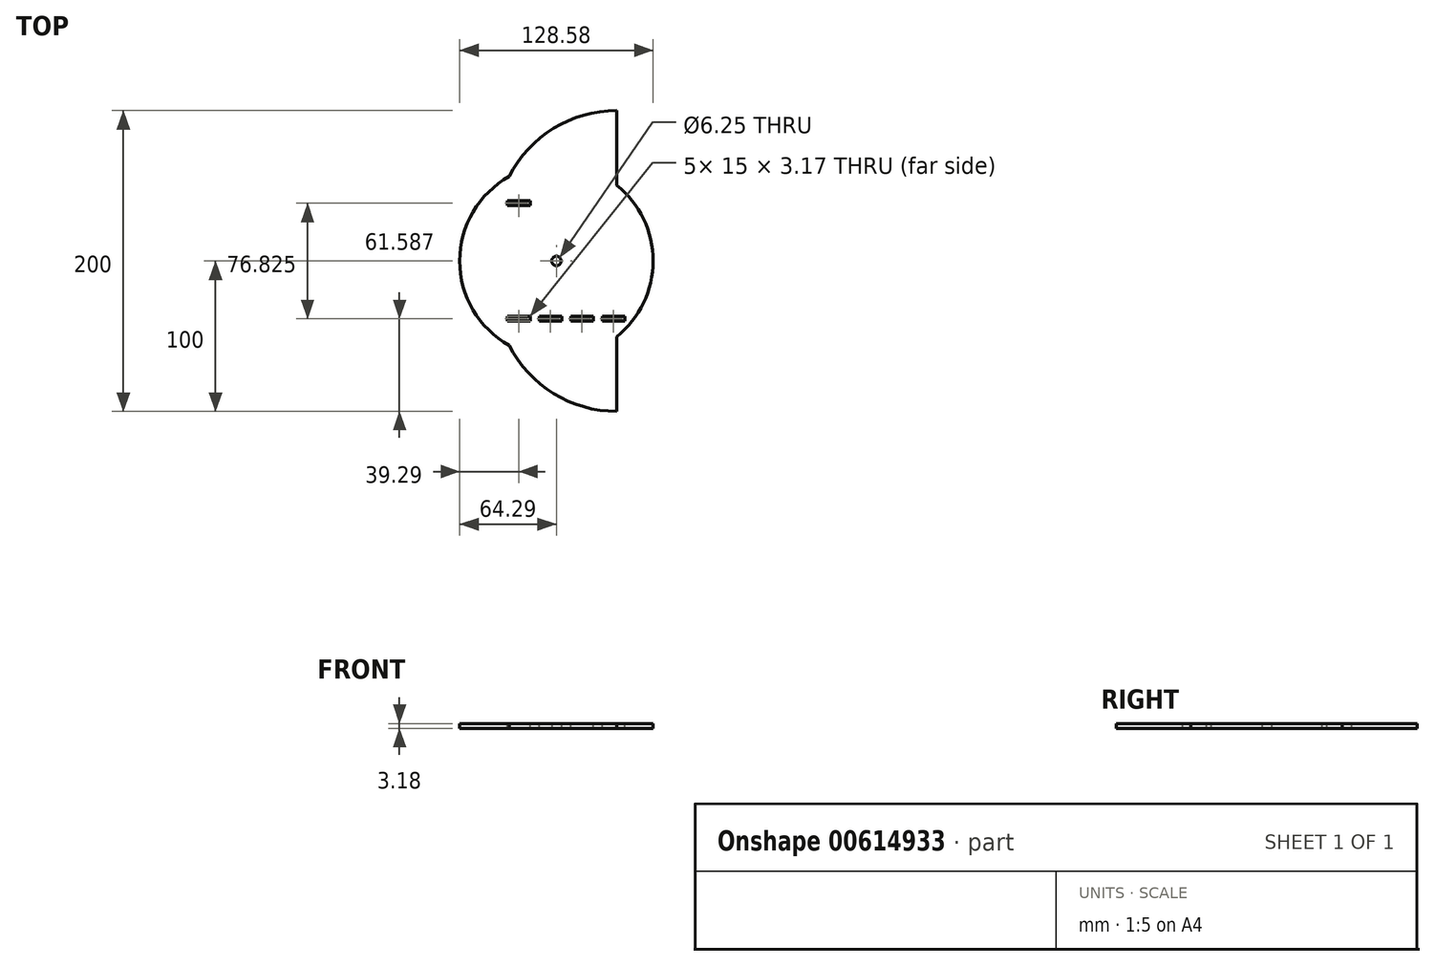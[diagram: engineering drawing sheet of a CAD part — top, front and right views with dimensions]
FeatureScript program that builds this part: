
annotation { "Feature Type Name" : "Feature", "Feature Type Description" : "" }
export const myFeature = defineFeature(function(context is Context, id is Id, definition is map)
    precondition{}
    {
        {
            var Q0;
            Q0=qCreatedBy(makeId("Top.planeOp"),FACE);
            var sketch = newSketch(context, id + "F0", { "sketchPlane" : qUnion([Q0])});
            skCircle(sketch, "E0", {"center": v(0, 0) * mm, "radius": 3.12 * mm});
            skCircle(sketch, "E1", {"center": v(0, 0) * mm, "radius": 64.29 * mm});
            skLineSegment(sketch, "E2.bottom", {"start": v(40, -100) * mm, "end": v(40, -100) * mm});
            skLineSegment(sketch, "E2.top", {"start": v(40, 100) * mm, "end": v(40, 100) * mm});
            skLineSegment(sketch, "E2.left", {"start": v(40, -100) * mm, "end": v(40, 100) * mm});
            skLineSegment(sketch, "E2.right", {"start": v(-40, -20) * mm, "end": v(-40, 20) * mm});
            skPoint(sketch, "E3.visualSharp", {"position": v(-40, 100) * mm});
            skArc(sketch, "E3.filletArc", {"start": v(40, 100) * mm, "mid": v(-16.57, 76.57) * mm, "end": v(-40, 20) * mm});
            skPoint(sketch, "E4.visualSharp", {"position": v(-40, -100) * mm});
            skArc(sketch, "E4.filletArc", {"start": v(-40, -20) * mm, "mid": v(-16.57, -76.57) * mm, "end": v(40, -100) * mm});
            skSolve(sketch);
        }
        {
            var Q0;
            Q0=qSketchRegion(id+"F0",true);
            extrude(context, id + "F1", {"entities" : qUnion([Q0]), "depth" : 0.12 * 25.4 * mm, "offsetDistance" : 25 * mm});
        }
        {
            var Q0;
            Q0=makeQuery(id+"F1.opExtrude","CAP_FACE",FACE,{"disambiguationData":[OSD([sQuery(id+"F0.wireOp",EDGE,"E0"),sQuery(id+"F0.wireOp",EDGE,"E1")])],"isStart":false});
            var sketch = newSketch(context, id + "F2", { "sketchPlane" : qUnion([Q0])});
            skLineSegment(sketch, "E5", {"start": v(17, 40) * mm, "end": v(-11.5, 40) * mm});
            skLineSegment(sketch, "E6", {"start": v(17, 40) * mm, "end": v(45.5, 40) * mm});
            skLineSegment(sketch, "E7.bottom", {"start": v(-11.5, 40) * mm, "end": v(3.5, 40) * mm});
            skLineSegment(sketch, "E7.top", {"start": v(-11.5, 36.83) * mm, "end": v(3.5, 36.83) * mm});
            skLineSegment(sketch, "E7.left", {"start": v(-11.5, 40) * mm, "end": v(-11.5, 36.83) * mm});
            skLineSegment(sketch, "E7.right", {"start": v(3.5, 40) * mm, "end": v(3.5, 36.83) * mm});
            skLineSegment(sketch, "E8.bottom", {"start": v(45.5, 40) * mm, "end": v(30.5, 40) * mm});
            skLineSegment(sketch, "E8.top", {"start": v(45.5, 36.83) * mm, "end": v(30.5, 36.82) * mm});
            skLineSegment(sketch, "E8.left", {"start": v(45.5, 40) * mm, "end": v(45.5, 36.83) * mm});
            skLineSegment(sketch, "E8.right", {"start": v(30.5, 40) * mm, "end": v(30.5, 36.83) * mm});
            skLineSegment(sketch, "E9.bottom", {"start": v(17, 40) * mm, "end": v(9.5, 40) * mm});
            skLineSegment(sketch, "E9.top", {"start": v(17, 36.82) * mm, "end": v(9.5, 36.82) * mm});
            skLineSegment(sketch, "E9.left", {"start": v(17, 40) * mm, "end": v(17, 36.83) * mm});
            skLineSegment(sketch, "E9.right", {"start": v(9.5, 40) * mm, "end": v(9.5, 36.83) * mm});
            skLineSegment(sketch, "E10.bottom", {"start": v(17, 40) * mm, "end": v(24.5, 40) * mm});
            skLineSegment(sketch, "E10.top", {"start": v(17, 36.83) * mm, "end": v(24.5, 36.83) * mm});
            skLineSegment(sketch, "E10.right", {"start": v(24.5, 40) * mm, "end": v(24.5, 36.83) * mm});
            skPoint(sketch, "E11.middle", {"position": v(17, 40) * mm});
            skLineSegment(sketch, "E12.MirrorCS", {"start": v(17, -40) * mm, "end": v(17, -36.83) * mm});
            skLineSegment(sketch, "E13.MirrorCS", {"start": v(30.5, -40) * mm, "end": v(30.5, -36.83) * mm});
            skLineSegment(sketch, "E14.MirrorCS", {"start": v(3.5, -40) * mm, "end": v(3.5, -36.83) * mm});
            skLineSegment(sketch, "E15.MirrorCS", {"start": v(-11.5, -40) * mm, "end": v(-11.5, -36.83) * mm});
            skLineSegment(sketch, "E16.MirrorCS", {"start": v(24.5, -40) * mm, "end": v(24.5, -36.83) * mm});
            skLineSegment(sketch, "E17.MirrorCS", {"start": v(45.5, -40) * mm, "end": v(45.5, -36.83) * mm});
            skLineSegment(sketch, "E18.MirrorCS", {"start": v(9.5, -40) * mm, "end": v(9.5, -36.83) * mm});
            skLineSegment(sketch, "E19.MirrorCS", {"start": v(17, -40) * mm, "end": v(24.5, -40) * mm});
            skLineSegment(sketch, "E20.MirrorCS", {"start": v(17, -36.82) * mm, "end": v(9.5, -36.82) * mm});
            skLineSegment(sketch, "E21.MirrorCS", {"start": v(17, -40) * mm, "end": v(9.5, -40) * mm});
            skLineSegment(sketch, "E22.MirrorCS", {"start": v(45.5, -36.83) * mm, "end": v(30.5, -36.82) * mm});
            skLineSegment(sketch, "E23.MirrorCS", {"start": v(-11.5, -36.83) * mm, "end": v(3.5, -36.83) * mm});
            skLineSegment(sketch, "E24.MirrorCS", {"start": v(-11.5, -40) * mm, "end": v(3.5, -40) * mm});
            skPoint(sketch, "E25.MirrorP", {"position": v(17, -40) * mm});
            skLineSegment(sketch, "E26.MirrorCS", {"start": v(17, -36.83) * mm, "end": v(24.5, -36.83) * mm});
            skLineSegment(sketch, "E27.MirrorCS", {"start": v(17, -40) * mm, "end": v(-11.5, -40) * mm});
            skLineSegment(sketch, "E28.MirrorCS", {"start": v(17, -40) * mm, "end": v(45.5, -40) * mm});
            skLineSegment(sketch, "E29.MirrorCS", {"start": v(17, -40) * mm, "end": v(17, 0) * mm});
            skLineSegment(sketch, "E30.MirrorCS", {"start": v(45.5, -40) * mm, "end": v(30.5, -40) * mm});
            skLineSegment(sketch, "E31", {"start": v(24.5, 40) * mm, "end": v(30.5, 40) * mm});
            skLineSegment(sketch, "E32", {"start": v(-11.5, 40) * mm, "end": v(-17.5, 40) * mm});
            skLineSegment(sketch, "E33", {"start": v(-17.5, 40) * mm, "end": v(-32.5, 40) * mm});
            skLineSegment(sketch, "E34", {"start": v(-17.5, 40) * mm, "end": v(-17.5, 36.83) * mm});
            skLineSegment(sketch, "E35", {"start": v(-17.5, 36.83) * mm, "end": v(-32.5, 36.83) * mm});
            skLineSegment(sketch, "E36", {"start": v(-32.5, 36.83) * mm, "end": v(-32.5, 40) * mm});
            skLineSegment(sketch, "E37", {"start": v(-11.5, -40) * mm, "end": v(-17.5, -40) * mm});
            skLineSegment(sketch, "E38", {"start": v(-17.5, -40) * mm, "end": v(-32.5, -40) * mm});
            skLineSegment(sketch, "E39", {"start": v(-32.5, -40) * mm, "end": v(-32.5, -36.83) * mm});
            skLineSegment(sketch, "E40", {"start": v(-32.5, -36.83) * mm, "end": v(-17.5, -36.83) * mm});
            skLineSegment(sketch, "E41", {"start": v(-17.5, -36.83) * mm, "end": v(-17.5, -40) * mm});
            skSolve(sketch);
        }
        {
            var Q0;
            Q0=makeQuery(id+"F2.imprint","IMPRINT",FACE,{"disambiguationData":[TD([[makeQuery(id+"F2.imprint","IMPRINT",EDGE,{"derivedFrom":sQuery(id+"F2.wireOp",EDGE,"9be99fbf-335f-4471-b1ea-c86e7e199887.bottom")}),-1.0]])]});
            var Q1;
            Q1=makeQuery(id+"F2.imprint","IMPRINT",FACE,{"disambiguationData":[TD([[makeQuery(id+"F2.imprint","IMPRINT",EDGE,{"derivedFrom":sQuery(id+"F2.wireOp",EDGE,"a2554bdb-a92a-45f0-9188-7e2be4d22b11.bottom")}),1.0]])]});
            var Q2;
            Q2=makeQuery(id+"F2.imprint","IMPRINT",FACE,{"disambiguationData":[TD([[makeQuery(id+"F2.imprint","IMPRINT",EDGE,{"derivedFrom":sQuery(id+"F2.wireOp",EDGE,"0acae45e-3260-4a4a-933d-839b9b166d6f.bottom")}),-1.0]])]});
            var Q3;
            Q3=makeQuery(id+"F2.imprint","IMPRINT",FACE,{"disambiguationData":[TD([[makeQuery(id+"F2.imprint","IMPRINT",EDGE,{"derivedFrom":sQuery(id+"F2.wireOp",EDGE,"af77130d-f040-469f-b1d9-c41bc226b897.bottom")}),1.0]])]});
            var Q4;
            {var subQ0=sQuery(id+"F2.wireOp",EDGE,"91671b91-2601-4e7c-b9c0-67f83fe829c40.MirrorCS");Q4=makeQuery(id+"F2.imprint","IMPRINT",FACE,{"disambiguationData":[TD([[makeQuery(id+"F2.imprint","IMPRINT",EDGE,{"derivedFrom":subQ0}),-1.0]])]});}
            var Q5;
            {var subQ4=sQuery(id+"F2.wireOp",EDGE,"91671b91-2601-4e7c-b9c0-67f83fe829c46.MirrorCS");Q5=makeQuery(id+"F2.imprint","IMPRINT",FACE,{"disambiguationData":[TD([[makeQuery(id+"F2.imprint","IMPRINT",EDGE,{"derivedFrom":subQ4}),1.0]])]});}
            var Q6;
            {var subQ0=sQuery(id+"F2.wireOp",EDGE,"91671b91-2601-4e7c-b9c0-67f83fe829c43.MirrorCS");Q6=makeQuery(id+"F2.imprint","IMPRINT",FACE,{"disambiguationData":[TD([[makeQuery(id+"F2.imprint","IMPRINT",EDGE,{"derivedFrom":subQ0}),-1.0]])]});}
            var Q7;
            Q7=makeQuery(id+"F2.imprint","IMPRINT",FACE,{"disambiguationData":[TD([[makeQuery(id+"F2.imprint","IMPRINT",EDGE,{"derivedFrom":sQuery(id+"F2.wireOp",EDGE,"E7.bottom")}),-1.0]])]});
            var Q8;
            {var subQ0=sQuery(id+"F2.wireOp",EDGE,"E9.bottom");Q8=makeQuery(id+"F2.imprint","IMPRINT",FACE,{"disambiguationData":[TD([[makeQuery(id+"F2.imprint","IMPRINT",EDGE,{"derivedFrom":subQ0}),1.0]])]});}
            var Q9;
            {var subQ0=sQuery(id+"F2.wireOp",EDGE,"E10.bottom");Q9=makeQuery(id+"F2.imprint","IMPRINT",FACE,{"disambiguationData":[TD([[makeQuery(id+"F2.imprint","IMPRINT",EDGE,{"derivedFrom":subQ0}),-1.0]])]});}
            var Q10;
            Q10=makeQuery(id+"F2.imprint","IMPRINT",FACE,{"disambiguationData":[TD([[makeQuery(id+"F2.imprint","IMPRINT",EDGE,{"derivedFrom":sQuery(id+"F2.wireOp",EDGE,"E8.bottom")}),1.0]])]});
            var Q11;
            {var subQ0=sQuery(id+"F2.wireOp",EDGE,"E14.MirrorCS");Q11=makeQuery(id+"F2.imprint","IMPRINT",FACE,{"disambiguationData":[TD([[makeQuery(id+"F2.imprint","IMPRINT",EDGE,{"derivedFrom":subQ0}),1.0]])]});}
            var Q12;
            {var subQ0=sQuery(id+"F2.wireOp",EDGE,"E16.MirrorCS");Q12=makeQuery(id+"F2.imprint","IMPRINT",FACE,{"disambiguationData":[TD([[makeQuery(id+"F2.imprint","IMPRINT",EDGE,{"derivedFrom":subQ0}),1.0]])]});}
            var Q13;
            Q13=makeQuery(id+"F2.imprint","IMPRINT",FACE,{"disambiguationData":[TD([[makeQuery(id+"F2.imprint","IMPRINT",EDGE,{"derivedFrom":sQuery(id+"F2.wireOp",EDGE,"E13.MirrorCS")}),-1.0]])]});
            var Q14;
            {var subQ0=sQuery(id+"F2.wireOp",EDGE,"E18.MirrorCS");Q14=makeQuery(id+"F2.imprint","IMPRINT",FACE,{"disambiguationData":[TD([[makeQuery(id+"F2.imprint","IMPRINT",EDGE,{"derivedFrom":subQ0}),-1.0]])]});}
            var Q15;
            Q15=makeQuery(id+"F2.imprint","IMPRINT",FACE,{"disambiguationData":[TD([[makeQuery(id+"F2.imprint","IMPRINT",EDGE,{"derivedFrom":sQuery(id+"F2.wireOp",EDGE,"E38")}),-1.0]])]});
            var Q16;
            Q16=makeQuery(id+"F2.imprint","IMPRINT",FACE,{"disambiguationData":[TD([[makeQuery(id+"F2.imprint","IMPRINT",EDGE,{"derivedFrom":sQuery(id+"F2.wireOp",EDGE,"E33")}),1.0]])]});
            extrude(context, id + "F3", {"entities" : qUnion([Q0, Q1, Q2, Q3, Q4, Q5, Q6, Q7, Q8, Q9, Q10, Q11, Q12, Q13, Q14, Q15, Q16]), "operationType" : NewBodyOperationType.REMOVE, "oppositeDirection" : true, "depth" : 25 * mm, "offsetDistance" : 25 * mm});
        }
    });
